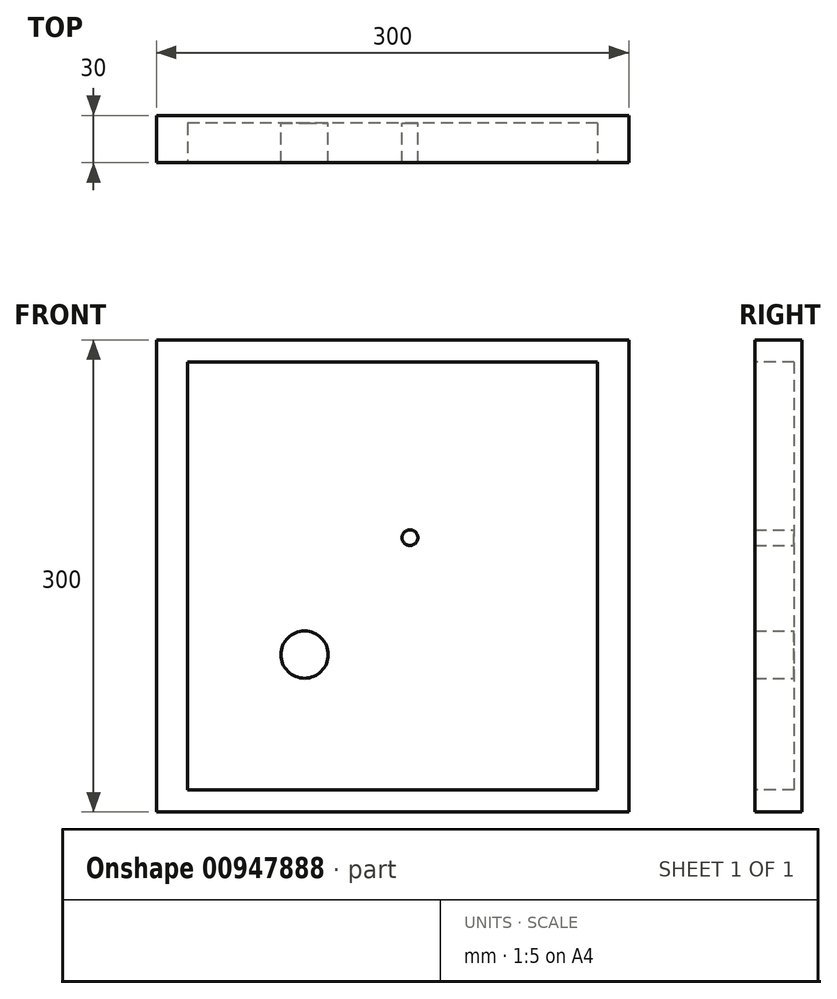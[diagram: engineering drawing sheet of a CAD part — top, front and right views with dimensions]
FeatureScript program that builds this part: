
annotation { "Feature Type Name" : "Feature", "Feature Type Description" : "" }
export const myFeature = defineFeature(function(context is Context, id is Id, definition is map)
    precondition{}
    {
        {
            var Q0;
            Q0=qCreatedBy(makeId("Front.planeOp"),FACE);
            var sketch = newSketch(context, id + "F0", { "sketchPlane" : qUnion([Q0])});
            skLineSegment(sketch, "E0.bottom", {"start": v(-150, 150) * mm, "end": v(150, 150) * mm});
            skLineSegment(sketch, "E0.top", {"start": v(-150, -150) * mm, "end": v(150, -150) * mm});
            skLineSegment(sketch, "E0.left", {"start": v(-150, 150) * mm, "end": v(-150, -150) * mm});
            skLineSegment(sketch, "E0.right", {"start": v(150, 150) * mm, "end": v(150, -150) * mm});
            skPoint(sketch, "E0.middle", {"position": v(0, 0) * mm});
            skSolve(sketch);
        }
        {
            var Q0;
            Q0 = qSketchRegion(id + "F0", true);
            var Q1;
            Q1=makeQuery(id+"F0.imprint","IMPRINT",FACE,{"disambiguationData":[TD([[makeQuery(id+"F0.imprint","IMPRINT",EDGE,{"derivedFrom":sQuery(id+"F0.wireOp",EDGE,"E0.bottom")}),-1.0]])]});
            extrude(context, id + "F1", {"entities" : qUnion([Q0, Q1]), "depth" : 30 * mm, "offsetDistance" : 25 * mm});
        }
        {
            var Q0;
            Q0=makeQuery(id+"F1.opExtrude","CAP_FACE",FACE,{"disambiguationData":[OSD([sQuery(id+"F0.wireOp",EDGE,"E0.bottom"),sQuery(id+"F0.wireOp",EDGE,"E0.top"),sQuery(id+"F0.wireOp",EDGE,"E0.left"),sQuery(id+"F0.wireOp",EDGE,"E0.right")])],"isStart":false});
            var sketch = newSketch(context, id + "F2", { "sketchPlane" : qUnion([Q0])});
            skLineSegment(sketch, "E1.bottom", {"start": v(130.26, 136) * mm, "end": v(-130.26, 136) * mm});
            skLineSegment(sketch, "E1.top", {"start": v(130.26, -136) * mm, "end": v(-130.26, -136) * mm});
            skLineSegment(sketch, "E1.left", {"start": v(130.26, 136) * mm, "end": v(130.26, -136) * mm});
            skLineSegment(sketch, "E1.right", {"start": v(-130.26, 136) * mm, "end": v(-130.26, -136) * mm});
            skPoint(sketch, "E1.middle", {"position": v(0, 0) * mm});
            skSolve(sketch);
        }
        {
            var Q0;
            Q0 = qSketchRegion(id + "F2", true);
            extrude(context, id + "F3", {"entities" : qUnion([Q0]), "operationType" : NewBodyOperationType.REMOVE, "oppositeDirection" : true, "depth" : 25 * mm, "offsetDistance" : 25 * mm});
        }
        {
            var Q0;
            Q0=makeQuery(id+"F3.boolean.opBoolean","COPY",FACE,{"derivedFrom":makeQuery(id+"F3.opExtrude","CAP_FACE",FACE,{"disambiguationData":[OSD([sQuery(id+"F2.wireOp",EDGE,"E1.bottom"),sQuery(id+"F2.wireOp",EDGE,"E1.top"),sQuery(id+"F2.wireOp",EDGE,"E1.left"),sQuery(id+"F2.wireOp",EDGE,"E1.right")])],"isStart":false})});
            var sketch = newSketch(context, id + "F4", { "sketchPlane" : qUnion([Q0])});
            skCircle(sketch, "E2", {"center": v(-55.92, -49.99) * mm, "radius": 15 * mm});
            skLineSegment(sketch, "E3", {"start": v(-55.92, -49.99) * mm, "end": v(11.03, 24.3) * mm});
            skCircle(sketch, "E4", {"center": v(11.03, 24.3) * mm, "radius": 5 * mm});
            skSolve(sketch);
        }
        {
            var Q0;
            Q0=makeQuery(id+"F4.imprint","IMPRINT",FACE,{"disambiguationData":[TD([[makeQuery(id+"F4.imprint","IMPRINT",EDGE,{"derivedFrom":sQuery(id+"F4.wireOp",EDGE,"E2")}),1.0]])]});
            var Q1;
            Q1=makeQuery(id+"F4.imprint","IMPRINT",FACE,{"disambiguationData":[TD([[makeQuery(id+"F4.imprint","IMPRINT",EDGE,{"derivedFrom":sQuery(id+"F4.wireOp",EDGE,"E4")}),1.0]])]});
            extrude(context, id + "F5", {"entities" : qUnion([Q0, Q1]), "operationType" : NewBodyOperationType.ADD, "depth" : 25 * mm, "offsetDistance" : 25 * mm});
        }
    });
